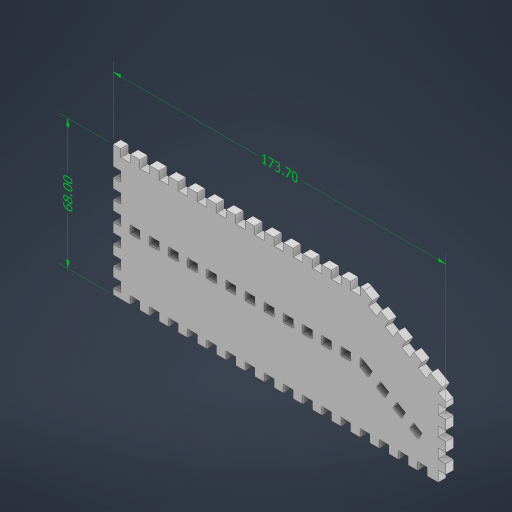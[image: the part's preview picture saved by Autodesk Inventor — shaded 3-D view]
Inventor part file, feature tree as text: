
AUTODESK INVENTOR PART (.ipt)
format: ipt  version: 2023 (Build 270158030, 158C)  size: 702,976 bytes
history: native  units: mm
features: extrude x5, sketch x5, other x3, projected_geometry x1
ambient origin geometry x8: Origin, YZ Plane, XZ Plane, XY Plane, X Axis, Y Axis, Z Axis, Center Point
bodies: Solid1 (feature_tree)
feature tree (14):
  other  "Annotations"
  extrude  "Extrusion1"  Depth=60.0mm
  sketch  "Sketch2"  dims[d2=47.0mm d3=30.0deg]
  extrude  "Extrusion2"  TaperAngle=30.0deg  [1 undecoded]
  extrude  "Extrusion3"  Depth=4.0mm TaperAngle=0.0deg
  extrude  "Extrusion4"  Depth=4.0mm
  extrude  "Extrusion5"  Depth=5.0mm
  sketch  "Sketch5"  dims[d9=120.0mm d11=10.0mm d12=10.0mm d14=10.0mm d16=5.0mm d17=4.0mm d18=50.0mm d20=10.0mm d21=10.0mm d23=10.0mm d25=7.0mm d26=5.0mm d27=4.0mm d28=120.0mm d30=10.0mm d31=10.0mm d33=10.0mm d35=5.0mm d36=30.0deg d37=4.0mm d38=40.0mm d40=10.0mm d41=10.0mm d43=10.0mm d45=5.0mm d46=4.0mm d47=170.0mm d49=10.0mm d50=10.0mm d52=10.0mm d54=4.0mm d55=0.0mm d56=4.0mm d57=0.0mm d58=4.0mm d59=10.0mm d60=4.0mm d61=5.0mm d62=60.0mm d64=10.0mm d65=10.0mm d67=10.0mm d69=4.0mm d70=0.0mm d71=5.0mm d72=5.0mm d73=4.0mm d74=4.0mm d75=5.0mm d76=30.0mm d78=10.0mm d79=10.0mm d81=10.0mm d83=4.0mm d84=0.0mm d85=2.396448mm d86=5.019131mm d87=68.0mm d88=5.652543mm d89=4.315711mm d90=173.703194mm]
  sketch  "Sketch1"  dims[d0=172.0mm d1=60.0mm]
  sketch  "Sketch3"  dims[d4=125.0mm d5=4.0mm d6=0.0mm]
  sketch  "Sketch4"  dims[d7=5.0mm d8=4.0mm]
  projected_geometry  "Projected Loop1"
  other  "Linear Dimension 1"
  other  "Linear Dimension 2"
note: 1 required parameter value undecoded (feature->parameter linkage not recoverable at this tier; creation-order binding heuristic only, values carry confidence <= 0.55)
